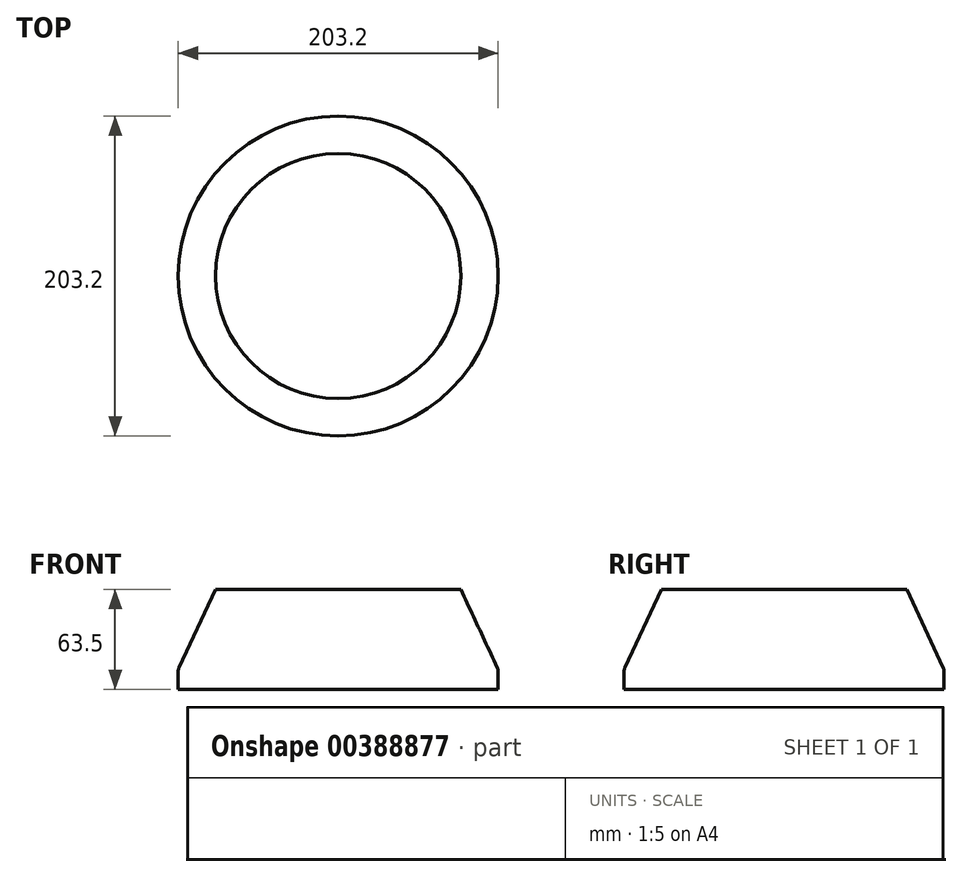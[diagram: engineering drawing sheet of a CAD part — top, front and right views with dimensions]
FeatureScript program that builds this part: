
annotation { "Feature Type Name" : "Feature", "Feature Type Description" : "" }
export const myFeature = defineFeature(function(context is Context, id is Id, definition is map)
    precondition{}
    {
        {
            var Q0;
            Q0=qCreatedBy(makeId("Top.planeOp"),FACE);
            var sketch = newSketch(context, id + "F0", { "sketchPlane" : qUnion([Q0])});
            skCircle(sketch, "E0", {"center": v(0, 0) * mm, "radius": 101.6 * mm});
            skSolve(sketch);
        }
        {
            var Q0;
            Q0 = qSketchRegion(id + "F0", true);
            extrude(context, id + "F1", {"entities" : qUnion([Q0]), "depth" : 12.7 * mm});
        }
        {
            var Q0;
            Q0=makeQuery(id+"F1.opExtrude","CAP_FACE",FACE,{"disambiguationData":[OSD([sQuery(id+"F0.wireOp",EDGE,"E0")])],"isStart":false});
            extrude(context, id + "F2", {"entities" : qUnion([Q0]), "operationType" : NewBodyOperationType.ADD, "depth" : 50.8 * mm, "hasDraft" : true, "draftAngle" : 25 * degree, "draftPullDirection" : true});
        }
        {
            var Q0;
            {var subQ0=sQuery(id+"F0.wireOp",EDGE,"E0");Q0=makeQuery(id+"F2.boolean.opBoolean","MERGE",EDGE,{"derivedFrom":[makeQuery(id+"F1.opExtrude","CAP_EDGE",EDGE,{"disambiguationData":[OSD([subQ0])],"isStart":false}),makeQuery(id+"F2.opExtrude","CAP_EDGE",EDGE,{"disambiguationData":[OSD([subQ0])],"isStart":true})]});}
            fillet(context, id + "F3", {"entities" : qUnion([Q0]), "radius" : 6.35 * mm, "tangentPropagation" : true, "allowEdgeOverflow" : false});
        }
    });
